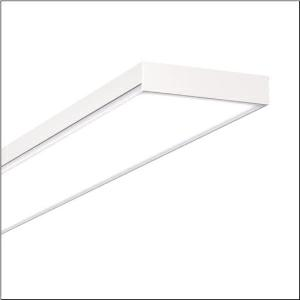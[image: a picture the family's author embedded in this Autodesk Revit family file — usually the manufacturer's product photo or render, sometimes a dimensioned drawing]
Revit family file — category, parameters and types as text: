
# Revit family: apollon_r__31_surface_51mp25wm2341w_ff2a
name_source: partatom
category: Lighting Fixtures
units: mm (PartAtom-declared; Revit-internal decimal feet)

## family parameters
Cut with Voids When Loaded = No
Host = Face
Light Source = No
Part Type = Normal
Room Calculation Point = No
Round Connector Dimension = Use Diameter
Shared = No

## types (1)
- Apollon® 31 Surface (1 x LED, 3600 lm, 27 W, 3000K)
    Apparent Load = 27 VA
    CIE Flux Codes = 61 87 97 97 100
    Color Rendering = 80
    Color Temperature = 3000K
    Default Elevation = 1800 mm
    Description = Apollon® 31 Surface, office luminaire, primary optical cover: micro prismatic cover, of PMMA, light emission: direct distribution, primary light characteristic: symmetric, installation type: surface-mounted, LED, rated luminous flux: 3.600lm, luminous efficacy: 132lm/W, light colour: 830, colour temperature: 3000K, control gear: ECG Multilumen, with terminal, 3-pole, mains connection: 220..240V, AC, 50/60Hz, rated input power: 27W, housing, of sheet steel, coil coated, traffic white (RAL 9016), length: 1.245mm, width: 200mm, height: 44mm, protection rating (complete): IP20, insulation class (complete): insulation class II (safety insulation), certification: CE, impact resistance: IK02, permissible operating ambient temperature: -20..+40°C, packaging unit: 1 piece
    Height = 44 mm
    Lamp = 1 x LED
    Lamp Light Flux = 3600 lm
    Lamp Power = 27 W
    Lamp count = 1
    Length = 1245 mm
    Luminous efficacy = 133 lm/W
    Manufacturer = Siteco
    ModVariant = No
    Model = 51MP25WM2341W
    Mounting Place = Ceiling
    Mounting Type = Surface mounted
    Number of Poles = 1
    OnlyDefault = Yes
    Power Factor = 1
    Product Name = Apollon® 31 Surface
    Product group = office luminaire | ceiling mounted
    ProductGroupID = 304
    Protection Class = Protection class II
    Protection Degree = IP 20
    RLX_Detail_Level = 1
    RLX_Emergency_Light_Flux = 0 lm
    RLX_Emergency_Type = 0
    RLX_Emergency_Type_DB = No
    RlxData = <blob elided: 20741 chars, md5=8e94d98b>
    Socket = socket
    Standby Power = 0 W
    System Light Flux = 3600 lm
    System Power = 27 W
    Type Comments = Product without accessories
    Type Image = l_1007095.jpg
    URL = http://relux.com
    VarID = ---
    Voltage = 0 V
    Weight = 0.00 kg
    Width = 200 mm  [stored 0.656168 ft]

note: [stored X ft] marks values corroborated as IEEE doubles in the binary element streams (Revit-internal decimal feet)

## geometry (parser evidence)
native form markers: Blend x4, Sweep x10
no freeform markers — native parametric forms only
